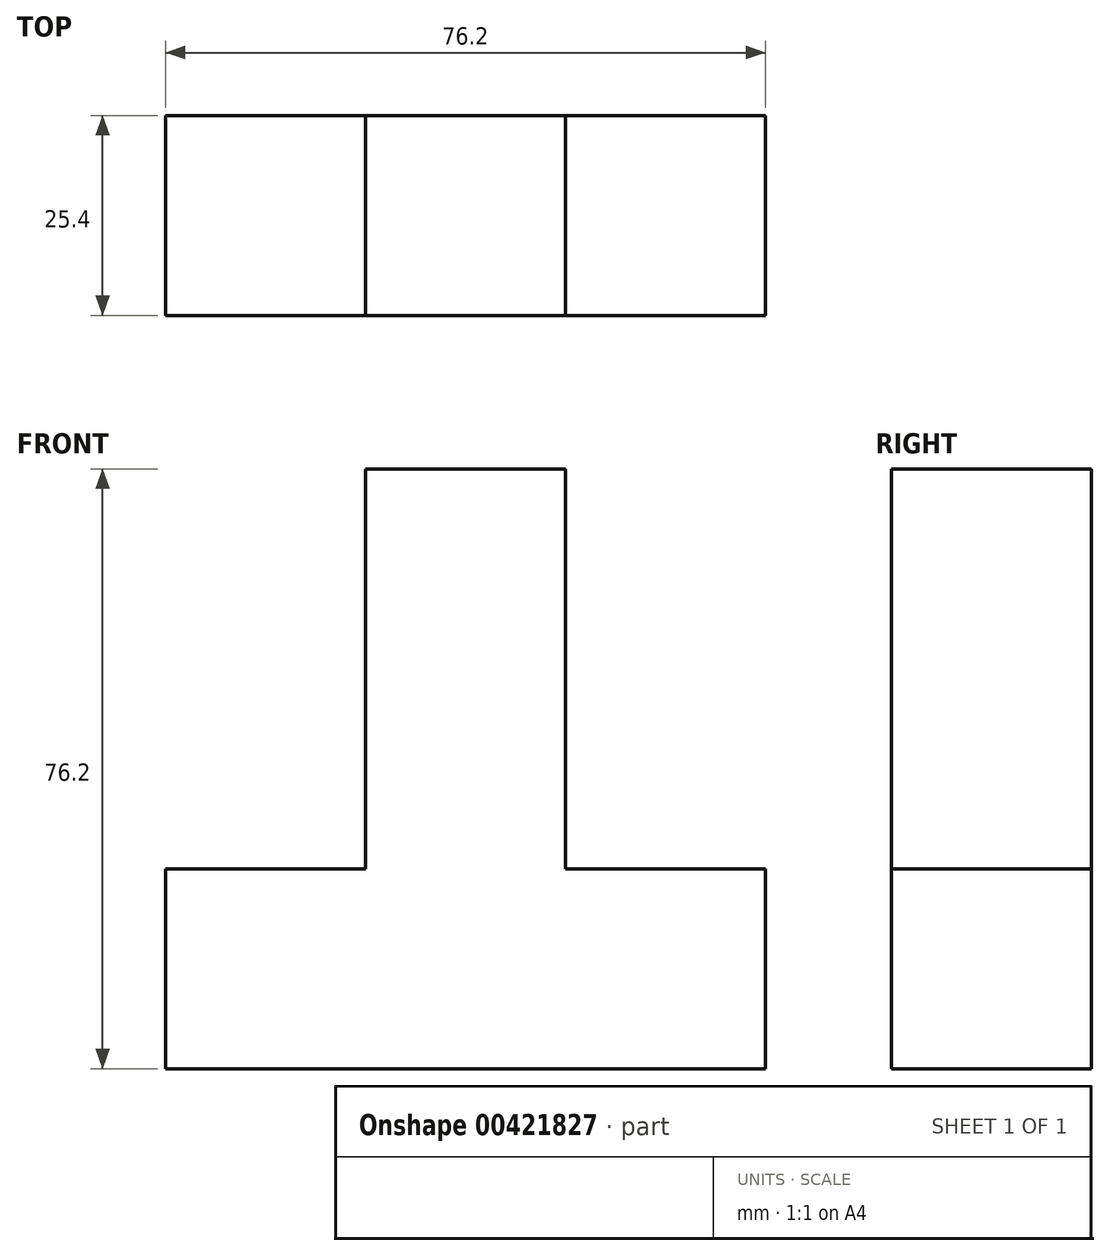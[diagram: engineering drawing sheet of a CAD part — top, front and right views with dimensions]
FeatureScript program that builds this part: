
annotation { "Feature Type Name" : "Feature", "Feature Type Description" : "" }
export const myFeature = defineFeature(function(context is Context, id is Id, definition is map)
    precondition{}
    {
        {
            var Q0;
            Q0=qCreatedBy(makeId("Front.planeOp"),FACE);
            var sketch = newSketch(context, id + "F0", { "sketchPlane" : qUnion([Q0])});
            skLineSegment(sketch, "E0", {"start": v(0, 0) * mm, "end": v(-76.2, 0) * mm});
            skLineSegment(sketch, "E1", {"start": v(-76.2, 0) * mm, "end": v(-76.2, 25.4) * mm});
            skLineSegment(sketch, "E2", {"start": v(-76.2, 25.4) * mm, "end": v(-50.8, 25.4) * mm});
            skLineSegment(sketch, "E3", {"start": v(-50.8, 25.4) * mm, "end": v(-50.8, 76.2) * mm});
            skLineSegment(sketch, "E4", {"start": v(-50.8, 76.2) * mm, "end": v(-25.4, 76.2) * mm});
            skLineSegment(sketch, "E5", {"start": v(-25.4, 76.2) * mm, "end": v(-25.4, 25.4) * mm});
            skLineSegment(sketch, "E6", {"start": v(-25.4, 25.4) * mm, "end": v(0, 25.4) * mm});
            skLineSegment(sketch, "E7", {"start": v(0, 25.4) * mm, "end": v(0, 0) * mm});
            skSolve(sketch);
        }
        {
            var Q0;
            Q0 = qSketchRegion(id + "F0", true);
            extrude(context, id + "F1", {"entities" : qUnion([Q0]), "depth" : 25.4 * mm});
        }
    });
